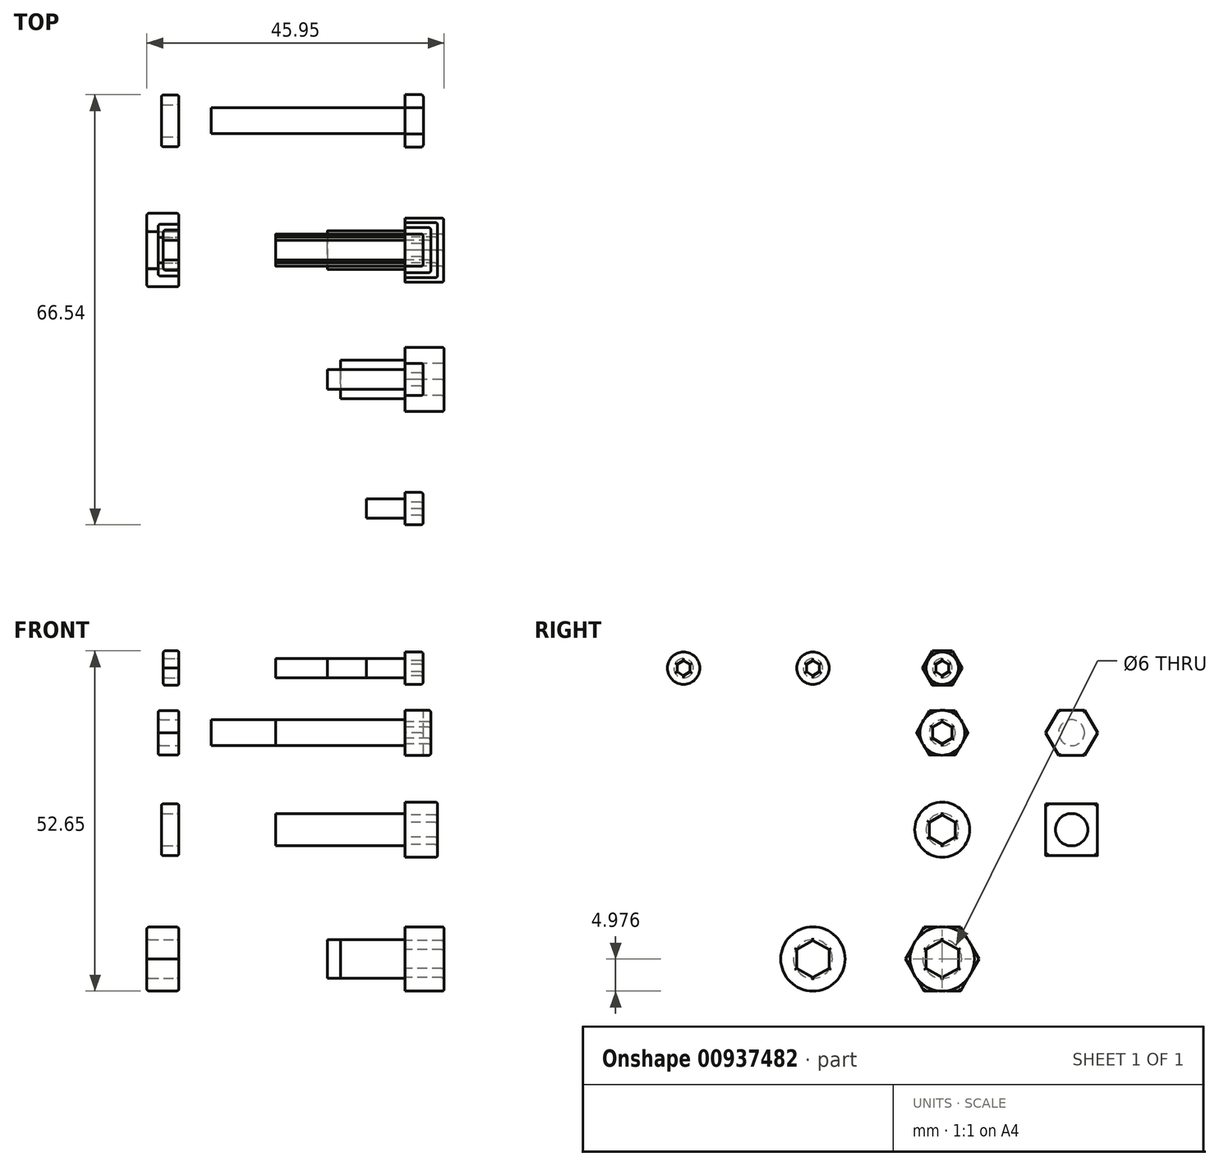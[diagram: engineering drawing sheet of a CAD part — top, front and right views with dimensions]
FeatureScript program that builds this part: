
annotation { "Feature Type Name" : "Feature", "Feature Type Description" : "" }
export const myFeature = defineFeature(function(context is Context, id is Id, definition is map)
    precondition{}
    {
        {
            var Q0;
            Q0=qCreatedBy(makeId("Right.planeOp"),FACE);
            var sketch = newSketch(context, id + "F0", { "sketchPlane" : qUnion([Q0])});
            skCircle(sketch, "E0.cCircle", {"center": v(-28.35, 39.66) * mm, "radius": 2.67 * mm, "construction": true});
            skLineSegment(sketch, "E0.0", {"start": v(-26.81, 36.98) * mm, "end": v(-29.9, 36.98) * mm});
            skLineSegment(sketch, "E0.1", {"start": v(-29.9, 36.98) * mm, "end": v(-31.44, 39.66) * mm});
            skLineSegment(sketch, "E0.2", {"start": v(-31.44, 39.66) * mm, "end": v(-29.9, 42.33) * mm});
            skLineSegment(sketch, "E0.3", {"start": v(-29.9, 42.33) * mm, "end": v(-26.81, 42.33) * mm});
            skLineSegment(sketch, "E0.4", {"start": v(-26.81, 42.33) * mm, "end": v(-25.27, 39.66) * mm});
            skLineSegment(sketch, "E0.5", {"start": v(-25.27, 39.66) * mm, "end": v(-26.81, 36.98) * mm});
            skPoint(sketch, "E0.0.midPoint", {"position": v(-28.35, 36.98) * mm});
            skCircle(sketch, "E1.cCircle", {"center": v(-28.35, 29.66) * mm, "radius": 3.45 * mm, "construction": true});
            skLineSegment(sketch, "E1.0", {"start": v(-26.36, 26.2) * mm, "end": v(-30.35, 26.2) * mm});
            skLineSegment(sketch, "E1.1", {"start": v(-30.35, 26.2) * mm, "end": v(-32.34, 29.66) * mm});
            skLineSegment(sketch, "E1.2", {"start": v(-32.34, 29.66) * mm, "end": v(-30.35, 33.1) * mm});
            skLineSegment(sketch, "E1.3", {"start": v(-30.35, 33.1) * mm, "end": v(-26.36, 33.1) * mm});
            skLineSegment(sketch, "E1.4", {"start": v(-26.36, 33.1) * mm, "end": v(-24.37, 29.66) * mm});
            skLineSegment(sketch, "E1.5", {"start": v(-24.37, 29.66) * mm, "end": v(-26.36, 26.2) * mm});
            skPoint(sketch, "E1.0.midPoint", {"position": v(-28.35, 26.2) * mm});
            skCircle(sketch, "E2.cCircle", {"center": v(-28.35, -5.34) * mm, "radius": 4.92 * mm, "construction": true});
            skLineSegment(sketch, "E2.0", {"start": v(-25.51, -10.27) * mm, "end": v(-31.2, -10.27) * mm});
            skLineSegment(sketch, "E2.1", {"start": v(-31.2, -10.27) * mm, "end": v(-34.04, -5.34) * mm});
            skLineSegment(sketch, "E2.2", {"start": v(-34.04, -5.34) * mm, "end": v(-31.2, -0.42) * mm});
            skLineSegment(sketch, "E2.3", {"start": v(-31.2, -0.42) * mm, "end": v(-25.51, -0.42) * mm});
            skLineSegment(sketch, "E2.4", {"start": v(-25.51, -0.42) * mm, "end": v(-22.67, -5.34) * mm});
            skLineSegment(sketch, "E2.5", {"start": v(-22.67, -5.34) * mm, "end": v(-25.51, -10.27) * mm});
            skPoint(sketch, "E2.0.midPoint", {"position": v(-28.35, -10.27) * mm});
            skCircle(sketch, "E3", {"center": v(-28.35, 39.66) * mm, "radius": 1.5 * mm});
            skCircle(sketch, "E4", {"center": v(-28.35, 29.66) * mm, "radius": 2 * mm});
            skCircle(sketch, "E5", {"center": v(-28.35, -5.34) * mm, "radius": 3 * mm});
            skLineSegment(sketch, "E6.bottom", {"start": v(-4.35, 18.66) * mm, "end": v(-12.35, 18.66) * mm});
            skLineSegment(sketch, "E6.top", {"start": v(-4.35, 10.66) * mm, "end": v(-12.35, 10.66) * mm});
            skLineSegment(sketch, "E6.left", {"start": v(-4.35, 18.66) * mm, "end": v(-4.35, 10.66) * mm});
            skLineSegment(sketch, "E6.right", {"start": v(-12.35, 18.66) * mm, "end": v(-12.35, 10.66) * mm});
            skCircle(sketch, "E7", {"center": v(-8.35, 14.66) * mm, "radius": 2.5 * mm});
            skLineSegment(sketch, "E8", {"start": v(-28.35, 48.47) * mm, "end": v(-28.35, -22.46) * mm, "construction": true});
            skLineSegment(sketch, "E9", {"start": v(-8.35, 48.47) * mm, "end": v(-8.35, -22.46) * mm, "construction": true});
            skPoint(sketch, "E10", {"position": v(-28.35, 14.66) * mm});
            skSolve(sketch);
        }
        {
            var Q0;
            Q0=makeQuery(id+"F0.imprint","IMPRINT",FACE,{"disambiguationData":[TD([[makeQuery(id+"F0.imprint","IMPRINT",EDGE,{"derivedFrom":sQuery(id+"F0.wireOp",EDGE,"E0.0")}),-1.0]])]});
            extrude(context, id + "F1", {"entities" : qUnion([Q0]), "oppositeDirection" : true, "depth" : 2.4 * mm, "offsetDistance" : 25 * mm});
        }
        {
            var Q0;
            Q0=makeQuery(id+"F0.imprint","IMPRINT",FACE,{"disambiguationData":[TD([[makeQuery(id+"F0.imprint","IMPRINT",EDGE,{"derivedFrom":sQuery(id+"F0.wireOp",EDGE,"E1.0")}),-1.0]])]});
            extrude(context, id + "F2", {"entities" : qUnion([Q0]), "oppositeDirection" : true, "depth" : 3.2 * mm, "offsetDistance" : 25 * mm});
        }
        {
            var Q0;
            Q0=makeQuery(id+"F0.imprint","IMPRINT",FACE,{"disambiguationData":[TD([[makeQuery(id+"F0.imprint","IMPRINT",EDGE,{"derivedFrom":sQuery(id+"F0.wireOp",EDGE,"E2.0")}),-1.0]])]});
            extrude(context, id + "F3", {"entities" : qUnion([Q0]), "oppositeDirection" : true, "depth" : 4.95 * mm, "offsetDistance" : 25 * mm});
        }
        {
            var Q0;
            Q0=makeQuery(id+"F0.imprint","IMPRINT",FACE,{"disambiguationData":[TD([[makeQuery(id+"F0.imprint","IMPRINT",EDGE,{"derivedFrom":sQuery(id+"F0.wireOp",EDGE,"E6.bottom")}),1.0]])]});
            extrude(context, id + "F4", {"entities" : qUnion([Q0]), "oppositeDirection" : true, "depth" : 2.7 * mm, "offsetDistance" : 25 * mm});
        }
        {
            var Q0;
            Q0=qCreatedBy(makeId("Right.planeOp"),FACE);
            cPlane(context, id + "F5", {"entities" : qUnion([Q0]), "cplaneType" : CPlaneType.OFFSET, "offset" : 35 * mm, "width" : 150 * mm, "height" : 150 * mm});
        }
        {
            var Q0;
            Q0=qCreatedBy(id+"F5.planeOp",FACE);
            var sketch = newSketch(context, id + "F6", { "sketchPlane" : qUnion([Q0])});
            skPoint(sketch, "E11.0", {"position": v(-28.35, 39.66) * mm});
            skPoint(sketch, "E11.1", {"position": v(-28.35, 29.66) * mm});
            skPoint(sketch, "E11.2", {"position": v(-28.35, -5.34) * mm});
            skCircle(sketch, "E12", {"center": v(-28.35, 39.66) * mm, "radius": 1.5 * mm});
            skCircle(sketch, "E13", {"center": v(-28.35, 29.66) * mm, "radius": 2 * mm});
            skCircle(sketch, "E14", {"center": v(-28.35, -5.34) * mm, "radius": 3 * mm});
            skCircle(sketch, "E15", {"center": v(-28.35, 39.66) * mm, "radius": 2.5 * mm});
            skCircle(sketch, "E16", {"center": v(-28.35, 29.66) * mm, "radius": 3.48 * mm});
            skCircle(sketch, "E17", {"center": v(-28.35, -5.34) * mm, "radius": 4.97 * mm});
            skCircle(sketch, "E18.cCircle", {"center": v(-28.35, -5.34) * mm, "radius": 2.5 * mm, "construction": true});
            skLineSegment(sketch, "E18.0", {"start": v(-25.85, -3.9) * mm, "end": v(-25.85, -6.79) * mm});
            skLineSegment(sketch, "E18.1", {"start": v(-25.85, -6.79) * mm, "end": v(-28.35, -8.23) * mm});
            skLineSegment(sketch, "E18.2", {"start": v(-28.35, -8.23) * mm, "end": v(-30.85, -6.79) * mm});
            skLineSegment(sketch, "E18.3", {"start": v(-30.85, -6.79) * mm, "end": v(-30.85, -3.9) * mm});
            skLineSegment(sketch, "E18.4", {"start": v(-30.85, -3.9) * mm, "end": v(-28.35, -2.46) * mm});
            skLineSegment(sketch, "E18.5", {"start": v(-28.35, -2.46) * mm, "end": v(-25.85, -3.9) * mm});
            skPoint(sketch, "E18.0.midPoint", {"position": v(-25.85, -5.34) * mm});
            skCircle(sketch, "E19.cCircle", {"center": v(-28.35, 29.66) * mm, "radius": 1.5 * mm, "construction": true});
            skLineSegment(sketch, "E19.0", {"start": v(-26.85, 30.52) * mm, "end": v(-26.85, 28.79) * mm});
            skLineSegment(sketch, "E19.1", {"start": v(-26.85, 28.79) * mm, "end": v(-28.35, 27.92) * mm});
            skLineSegment(sketch, "E19.2", {"start": v(-28.35, 27.92) * mm, "end": v(-29.85, 28.79) * mm});
            skLineSegment(sketch, "E19.3", {"start": v(-29.85, 28.79) * mm, "end": v(-29.85, 30.52) * mm});
            skLineSegment(sketch, "E19.4", {"start": v(-29.85, 30.52) * mm, "end": v(-28.35, 31.39) * mm});
            skLineSegment(sketch, "E19.5", {"start": v(-28.35, 31.39) * mm, "end": v(-26.85, 30.52) * mm});
            skPoint(sketch, "E19.0.midPoint", {"position": v(-26.85, 29.66) * mm});
            skCircle(sketch, "E20.cCircle", {"center": v(-28.35, 39.66) * mm, "radius": 1 * mm, "construction": true});
            skLineSegment(sketch, "E20.0", {"start": v(-27.35, 40.23) * mm, "end": v(-27.35, 39.08) * mm});
            skLineSegment(sketch, "E20.1", {"start": v(-27.35, 39.08) * mm, "end": v(-28.35, 38.5) * mm});
            skLineSegment(sketch, "E20.2", {"start": v(-28.35, 38.5) * mm, "end": v(-29.35, 39.08) * mm});
            skLineSegment(sketch, "E20.3", {"start": v(-29.35, 39.08) * mm, "end": v(-29.35, 40.23) * mm});
            skLineSegment(sketch, "E20.4", {"start": v(-29.35, 40.23) * mm, "end": v(-28.35, 40.81) * mm});
            skLineSegment(sketch, "E20.5", {"start": v(-28.35, 40.81) * mm, "end": v(-27.35, 40.23) * mm});
            skPoint(sketch, "E20.0.midPoint", {"position": v(-27.35, 39.66) * mm});
            skPoint(sketch, "E21", {"position": v(-8.35, 29.66) * mm});
            skCircle(sketch, "E22", {"center": v(-8.35, 29.66) * mm, "radius": 2 * mm});
            skCircle(sketch, "E23.cCircle", {"center": v(-8.35, 29.66) * mm, "radius": 3.5 * mm, "construction": true});
            skLineSegment(sketch, "E23.0", {"start": v(-10.38, 33.16) * mm, "end": v(-6.33, 33.16) * mm});
            skLineSegment(sketch, "E23.1", {"start": v(-6.33, 33.16) * mm, "end": v(-4.31, 29.66) * mm});
            skLineSegment(sketch, "E23.2", {"start": v(-4.31, 29.66) * mm, "end": v(-6.33, 26.16) * mm});
            skLineSegment(sketch, "E23.3", {"start": v(-6.33, 26.16) * mm, "end": v(-10.38, 26.16) * mm});
            skLineSegment(sketch, "E23.4", {"start": v(-10.38, 26.16) * mm, "end": v(-12.4, 29.66) * mm});
            skLineSegment(sketch, "E23.5", {"start": v(-12.4, 29.66) * mm, "end": v(-10.38, 33.16) * mm});
            skPoint(sketch, "E23.0.midPoint", {"position": v(-8.35, 33.16) * mm});
            skPoint(sketch, "E24.0", {"position": v(-8.35, 14.66) * mm});
            skPoint(sketch, "E25.0", {"position": v(-28.35, 14.66) * mm});
            skCircle(sketch, "E26", {"center": v(-28.35, 14.66) * mm, "radius": 2.5 * mm});
            skCircle(sketch, "E27", {"center": v(-28.35, 14.66) * mm, "radius": 4.25 * mm});
            skCircle(sketch, "E28.cCircle", {"center": v(-28.35, 14.66) * mm, "radius": 2 * mm, "construction": true});
            skLineSegment(sketch, "E28.0", {"start": v(-26.35, 15.81) * mm, "end": v(-26.35, 13.5) * mm});
            skLineSegment(sketch, "E28.1", {"start": v(-26.35, 13.5) * mm, "end": v(-28.35, 12.35) * mm});
            skLineSegment(sketch, "E28.2", {"start": v(-28.35, 12.35) * mm, "end": v(-30.35, 13.5) * mm});
            skLineSegment(sketch, "E28.3", {"start": v(-30.35, 13.5) * mm, "end": v(-30.35, 15.81) * mm});
            skLineSegment(sketch, "E28.4", {"start": v(-30.35, 15.81) * mm, "end": v(-28.35, 16.96) * mm});
            skLineSegment(sketch, "E28.5", {"start": v(-28.35, 16.96) * mm, "end": v(-26.35, 15.81) * mm});
            skPoint(sketch, "E28.0.midPoint", {"position": v(-26.35, 14.66) * mm});
            skPoint(sketch, "E29.0", {"position": v(-48.35, 39.66) * mm});
            skCircle(sketch, "E30", {"center": v(-48.35, 39.66) * mm, "radius": 1.5 * mm});
            skCircle(sketch, "E31", {"center": v(-48.35, 39.66) * mm, "radius": 2.5 * mm});
            skCircle(sketch, "E32.cCircle", {"center": v(-48.35, 39.66) * mm, "radius": 1 * mm, "construction": true});
            skLineSegment(sketch, "E32.0", {"start": v(-47.35, 40.23) * mm, "end": v(-47.35, 39.08) * mm});
            skLineSegment(sketch, "E32.1", {"start": v(-47.35, 39.08) * mm, "end": v(-48.35, 38.5) * mm});
            skLineSegment(sketch, "E32.2", {"start": v(-48.35, 38.5) * mm, "end": v(-49.35, 39.08) * mm});
            skLineSegment(sketch, "E32.3", {"start": v(-49.35, 39.08) * mm, "end": v(-49.35, 40.23) * mm});
            skLineSegment(sketch, "E32.4", {"start": v(-49.35, 40.23) * mm, "end": v(-48.35, 40.81) * mm});
            skLineSegment(sketch, "E32.5", {"start": v(-48.35, 40.81) * mm, "end": v(-47.35, 40.23) * mm});
            skPoint(sketch, "E32.0.midPoint", {"position": v(-47.35, 39.66) * mm});
            skPoint(sketch, "E33.2", {"position": v(-48.35, -5.34) * mm});
            skCircle(sketch, "E34", {"center": v(-48.35, -5.34) * mm, "radius": 3 * mm});
            skCircle(sketch, "E35", {"center": v(-48.35, -5.34) * mm, "radius": 4.97 * mm});
            skCircle(sketch, "E36.cCircle", {"center": v(-48.35, -5.34) * mm, "radius": 2.5 * mm, "construction": true});
            skLineSegment(sketch, "E36.0", {"start": v(-45.85, -3.9) * mm, "end": v(-45.85, -6.79) * mm});
            skLineSegment(sketch, "E36.1", {"start": v(-45.85, -6.79) * mm, "end": v(-48.35, -8.23) * mm});
            skLineSegment(sketch, "E36.2", {"start": v(-48.35, -8.23) * mm, "end": v(-50.85, -6.79) * mm});
            skLineSegment(sketch, "E36.3", {"start": v(-50.85, -6.79) * mm, "end": v(-50.85, -3.9) * mm});
            skLineSegment(sketch, "E36.4", {"start": v(-50.85, -3.9) * mm, "end": v(-48.35, -2.46) * mm});
            skLineSegment(sketch, "E36.5", {"start": v(-48.35, -2.46) * mm, "end": v(-45.85, -3.9) * mm});
            skPoint(sketch, "E36.0.midPoint", {"position": v(-45.85, -5.34) * mm});
            skPoint(sketch, "E37", {"position": v(-30.85, -5.34) * mm});
            skPoint(sketch, "E38.0", {"position": v(-68.35, 39.66) * mm});
            skCircle(sketch, "E39", {"center": v(-68.35, 39.66) * mm, "radius": 1.5 * mm});
            skCircle(sketch, "E40", {"center": v(-68.35, 39.66) * mm, "radius": 2.5 * mm});
            skCircle(sketch, "E41.cCircle", {"center": v(-68.35, 39.66) * mm, "radius": 1 * mm, "construction": true});
            skLineSegment(sketch, "E41.0", {"start": v(-67.35, 40.23) * mm, "end": v(-67.35, 39.08) * mm});
            skLineSegment(sketch, "E41.1", {"start": v(-67.35, 39.08) * mm, "end": v(-68.35, 38.5) * mm});
            skLineSegment(sketch, "E41.2", {"start": v(-68.35, 38.5) * mm, "end": v(-69.35, 39.08) * mm});
            skLineSegment(sketch, "E41.3", {"start": v(-69.35, 39.08) * mm, "end": v(-69.35, 40.23) * mm});
            skLineSegment(sketch, "E41.4", {"start": v(-69.35, 40.23) * mm, "end": v(-68.35, 40.81) * mm});
            skLineSegment(sketch, "E41.5", {"start": v(-68.35, 40.81) * mm, "end": v(-67.35, 40.23) * mm});
            skPoint(sketch, "E41.0.midPoint", {"position": v(-67.35, 39.66) * mm});
            skSolve(sketch);
        }
        {
            var Q0;
            Q0=makeQuery(id+"F6.imprint","IMPRINT",FACE,{"disambiguationData":[TD([[makeQuery(id+"F6.imprint","IMPRINT",EDGE,{"derivedFrom":sQuery(id+"F6.wireOp",EDGE,"E12")}),1.0]])]});
            var Q1;
            Q1=makeQuery(id+"F6.imprint","IMPRINT",FACE,{"disambiguationData":[TD([[makeQuery(id+"F6.imprint","IMPRINT",EDGE,{"derivedFrom":sQuery(id+"F6.wireOp",EDGE,"E20.0")}),-1.0]])]});
            extrude(context, id + "F7", {"entities" : qUnion([Q0, Q1]), "oppositeDirection" : true, "depth" : 20 * mm, "offsetDistance" : 25 * mm});
        }
        {
            var Q0;
            Q0=makeQuery(id+"F6.imprint","IMPRINT",FACE,{"disambiguationData":[TD([[makeQuery(id+"F6.imprint","IMPRINT",EDGE,{"derivedFrom":sQuery(id+"F6.wireOp",EDGE,"E13")}),1.0]])]});
            var Q1;
            Q1=makeQuery(id+"F6.imprint","IMPRINT",FACE,{"disambiguationData":[TD([[makeQuery(id+"F6.imprint","IMPRINT",EDGE,{"derivedFrom":sQuery(id+"F6.wireOp",EDGE,"E19.0")}),-1.0]])]});
            extrude(context, id + "F8", {"entities" : qUnion([Q0, Q1]), "oppositeDirection" : true, "depth" : 20 * mm, "offsetDistance" : 25 * mm});
        }
        {
            var Q0;
            Q0=makeQuery(id+"F6.imprint","IMPRINT",FACE,{"disambiguationData":[TD([[makeQuery(id+"F6.imprint","IMPRINT",EDGE,{"derivedFrom":sQuery(id+"F6.wireOp",EDGE,"E18.0")}),-1.0]])]});
            var Q1;
            Q1=makeQuery(id+"F6.imprint","IMPRINT",FACE,{"disambiguationData":[TD([[makeQuery(id+"F6.imprint","IMPRINT",EDGE,{"derivedFrom":sQuery(id+"F6.wireOp",EDGE,"E14")}),1.0]])]});
            extrude(context, id + "F9", {"entities" : qUnion([Q0, Q1]), "flatOperationType" : FlatOperationType.REMOVE, "oppositeDirection" : true, "depth" : 12 * mm, "offsetDistance" : 25 * mm, "domain" : OperationDomain.MODEL});
        }
        {
            var Q0;
            Q0=makeQuery(id+"F6.imprint","IMPRINT",FACE,{"disambiguationData":[TD([[makeQuery(id+"F6.imprint","IMPRINT",EDGE,{"derivedFrom":sQuery(id+"F6.wireOp",EDGE,"E12")}),-1.0]])]});
            var Q1;
            Q1=makeQuery(id+"F6.imprint","IMPRINT",FACE,{"disambiguationData":[TD([[makeQuery(id+"F6.imprint","IMPRINT",EDGE,{"derivedFrom":sQuery(id+"F6.wireOp",EDGE,"E12")}),1.0]])]});
            extrude(context, id + "F10", {"entities" : qUnion([Q0, Q1]), "operationType" : NewBodyOperationType.ADD, "flatOperationType" : FlatOperationType.REMOVE, "depth" : 2.75 * mm, "offsetDistance" : 25 * mm, "domain" : OperationDomain.MODEL});
        }
        {
            var Q0;
            Q0=makeQuery(id+"F6.imprint","IMPRINT",FACE,{"disambiguationData":[TD([[makeQuery(id+"F6.imprint","IMPRINT",EDGE,{"derivedFrom":sQuery(id+"F6.wireOp",EDGE,"E13")}),1.0]])]});
            var Q1;
            Q1=makeQuery(id+"F6.imprint","IMPRINT",FACE,{"disambiguationData":[TD([[makeQuery(id+"F6.imprint","IMPRINT",EDGE,{"derivedFrom":sQuery(id+"F6.wireOp",EDGE,"E13")}),-1.0]])]});
            extrude(context, id + "F11", {"entities" : qUnion([Q0, Q1]), "operationType" : NewBodyOperationType.ADD, "flatOperationType" : FlatOperationType.REMOVE, "depth" : 3.95 * mm, "offsetDistance" : 25 * mm, "domain" : OperationDomain.MODEL});
        }
        {
            var Q0;
            Q0=makeQuery(id+"F6.imprint","IMPRINT",FACE,{"disambiguationData":[TD([[makeQuery(id+"F6.imprint","IMPRINT",EDGE,{"derivedFrom":sQuery(id+"F6.wireOp",EDGE,"E14")}),1.0]])]});
            var Q1;
            Q1=makeQuery(id+"F6.imprint","IMPRINT",FACE,{"disambiguationData":[TD([[makeQuery(id+"F6.imprint","IMPRINT",EDGE,{"derivedFrom":sQuery(id+"F6.wireOp",EDGE,"E14")}),-1.0]])]});
            extrude(context, id + "F12", {"entities" : qUnion([Q0, Q1]), "operationType" : NewBodyOperationType.ADD, "depth" : 5.95 * mm, "offsetDistance" : 25 * mm});
        }
        {
            var Q0;
            Q0=makeQuery(id+"F6.imprint","IMPRINT",FACE,{"disambiguationData":[TD([[makeQuery(id+"F6.imprint","IMPRINT",EDGE,{"derivedFrom":sQuery(id+"F6.wireOp",EDGE,"E22")}),1.0]])]});
            var Q1;
            Q1=makeQuery(id+"F6.imprint","IMPRINT",FACE,{"disambiguationData":[TD([[makeQuery(id+"F6.imprint","IMPRINT",EDGE,{"derivedFrom":sQuery(id+"F6.wireOp",EDGE,"E22")}),-1.0]])]});
            extrude(context, id + "F13", {"entities" : qUnion([Q0, Q1]), "depth" : 2.8 * mm, "offsetDistance" : 25 * mm});
        }
        {
            var Q0;
            Q0=makeQuery(id+"F6.imprint","IMPRINT",FACE,{"disambiguationData":[TD([[makeQuery(id+"F6.imprint","IMPRINT",EDGE,{"derivedFrom":sQuery(id+"F6.wireOp",EDGE,"E22")}),1.0]])]});
            extrude(context, id + "F14", {"entities" : qUnion([Q0]), "operationType" : NewBodyOperationType.ADD, "oppositeDirection" : true, "depth" : 30 * mm, "offsetDistance" : 25 * mm});
        }
        {
            var Q0;
            Q0=makeQuery(id+"F6.imprint","IMPRINT",FACE,{"disambiguationData":[TD([[makeQuery(id+"F6.imprint","IMPRINT",EDGE,{"derivedFrom":sQuery(id+"F6.wireOp",EDGE,"E26")}),-1.0]])]});
            var Q1;
            Q1=makeQuery(id+"F6.imprint","IMPRINT",FACE,{"disambiguationData":[TD([[makeQuery(id+"F6.imprint","IMPRINT",EDGE,{"derivedFrom":sQuery(id+"F6.wireOp",EDGE,"E26")}),1.0]])]});
            extrude(context, id + "F15", {"entities" : qUnion([Q0, Q1]), "depth" : 5 * mm, "offsetDistance" : 25 * mm});
        }
        {
            var Q0;
            Q0=makeQuery(id+"F6.imprint","IMPRINT",FACE,{"disambiguationData":[TD([[makeQuery(id+"F6.imprint","IMPRINT",EDGE,{"derivedFrom":sQuery(id+"F6.wireOp",EDGE,"E26")}),1.0]])]});
            var Q1;
            Q1=makeQuery(id+"F6.imprint","IMPRINT",FACE,{"disambiguationData":[TD([[makeQuery(id+"F6.imprint","IMPRINT",EDGE,{"derivedFrom":sQuery(id+"F6.wireOp",EDGE,"E28.0")}),-1.0]])]});
            extrude(context, id + "F16", {"entities" : qUnion([Q0, Q1]), "operationType" : NewBodyOperationType.ADD, "oppositeDirection" : true, "depth" : 20 * mm, "offsetDistance" : 25 * mm});
        }
        {
            var Q0;
            Q0=makeQuery(id+"F6.imprint","IMPRINT",FACE,{"disambiguationData":[TD([[makeQuery(id+"F6.imprint","IMPRINT",EDGE,{"derivedFrom":sQuery(id+"F6.wireOp",EDGE,"E32.0")}),-1.0]])]});
            var Q1;
            Q1=makeQuery(id+"F6.imprint","IMPRINT",FACE,{"disambiguationData":[TD([[makeQuery(id+"F6.imprint","IMPRINT",EDGE,{"derivedFrom":sQuery(id+"F6.wireOp",EDGE,"E30")}),1.0]])]});
            extrude(context, id + "F17", {"entities" : qUnion([Q0, Q1]), "oppositeDirection" : true, "depth" : 12 * mm, "offsetDistance" : 25 * mm});
        }
        {
            var Q0;
            Q0=makeQuery(id+"F6.imprint","IMPRINT",FACE,{"disambiguationData":[TD([[makeQuery(id+"F6.imprint","IMPRINT",EDGE,{"derivedFrom":sQuery(id+"F6.wireOp",EDGE,"E30")}),1.0]])]});
            var Q1;
            Q1=makeQuery(id+"F6.imprint","IMPRINT",FACE,{"disambiguationData":[TD([[makeQuery(id+"F6.imprint","IMPRINT",EDGE,{"derivedFrom":sQuery(id+"F6.wireOp",EDGE,"E30")}),-1.0]])]});
            extrude(context, id + "F18", {"entities" : qUnion([Q0, Q1]), "operationType" : NewBodyOperationType.ADD, "depth" : 2.75 * mm, "offsetDistance" : 25 * mm});
        }
        {
            var Q0;
            Q0=makeQuery(id+"F6.imprint","IMPRINT",FACE,{"disambiguationData":[TD([[makeQuery(id+"F6.imprint","IMPRINT",EDGE,{"derivedFrom":sQuery(id+"F6.wireOp",EDGE,"E36.0")}),-1.0]])]});
            var Q1;
            Q1=makeQuery(id+"F6.imprint","IMPRINT",FACE,{"disambiguationData":[TD([[makeQuery(id+"F6.imprint","IMPRINT",EDGE,{"derivedFrom":sQuery(id+"F6.wireOp",EDGE,"E34")}),1.0]])]});
            extrude(context, id + "F19", {"entities" : qUnion([Q0, Q1]), "oppositeDirection" : true, "depth" : 10 * mm, "offsetDistance" : 25 * mm});
        }
        {
            var Q0;
            Q0=makeQuery(id+"F6.imprint","IMPRINT",FACE,{"disambiguationData":[TD([[makeQuery(id+"F6.imprint","IMPRINT",EDGE,{"derivedFrom":sQuery(id+"F6.wireOp",EDGE,"E34")}),1.0]])]});
            var Q1;
            Q1=makeQuery(id+"F6.imprint","IMPRINT",FACE,{"disambiguationData":[TD([[makeQuery(id+"F6.imprint","IMPRINT",EDGE,{"derivedFrom":sQuery(id+"F6.wireOp",EDGE,"E34")}),-1.0]])]});
            extrude(context, id + "F20", {"entities" : qUnion([Q0, Q1]), "operationType" : NewBodyOperationType.ADD, "depth" : 6 * mm, "offsetDistance" : 25 * mm});
        }
        {
            var Q0;
            Q0=makeQuery(id+"F6.imprint","IMPRINT",FACE,{"disambiguationData":[TD([[makeQuery(id+"F6.imprint","IMPRINT",EDGE,{"derivedFrom":sQuery(id+"F6.wireOp",EDGE,"E41.0")}),-1.0]])]});
            var Q1;
            Q1=makeQuery(id+"F6.imprint","IMPRINT",FACE,{"disambiguationData":[TD([[makeQuery(id+"F6.imprint","IMPRINT",EDGE,{"derivedFrom":sQuery(id+"F6.wireOp",EDGE,"E39")}),1.0]])]});
            extrude(context, id + "F21", {"entities" : qUnion([Q0, Q1]), "oppositeDirection" : true, "depth" : 6 * mm, "offsetDistance" : 25 * mm});
        }
        {
            var Q0;
            Q0=makeQuery(id+"F6.imprint","IMPRINT",FACE,{"disambiguationData":[TD([[makeQuery(id+"F6.imprint","IMPRINT",EDGE,{"derivedFrom":sQuery(id+"F6.wireOp",EDGE,"E39")}),1.0]])]});
            var Q1;
            Q1=makeQuery(id+"F6.imprint","IMPRINT",FACE,{"disambiguationData":[TD([[makeQuery(id+"F6.imprint","IMPRINT",EDGE,{"derivedFrom":sQuery(id+"F6.wireOp",EDGE,"E39")}),-1.0]])]});
            extrude(context, id + "F22", {"entities" : qUnion([Q0, Q1]), "operationType" : NewBodyOperationType.ADD, "depth" : 2.75 * mm, "offsetDistance" : 25 * mm});
        }
        {
            var Q0;
            Q0=makeQuery(id+"F2.opExtrude","CAP_FACE",FACE,{"disambiguationData":[OSD([sQuery(id+"F0.wireOp",EDGE,"E1.0"),sQuery(id+"F0.wireOp",EDGE,"E1.1"),sQuery(id+"F0.wireOp",EDGE,"E1.2"),sQuery(id+"F0.wireOp",EDGE,"E1.3"),sQuery(id+"F0.wireOp",EDGE,"E1.4"),sQuery(id+"F0.wireOp",EDGE,"E1.5"),sQuery(id+"F0.wireOp",EDGE,"E4")])],"isStart":false});
            var Q1;
            Q1=makeQuery(id+"F3.opExtrude","CAP_FACE",FACE,{"disambiguationData":[OSD([sQuery(id+"F0.wireOp",EDGE,"E2.0"),sQuery(id+"F0.wireOp",EDGE,"E2.1"),sQuery(id+"F0.wireOp",EDGE,"E2.2"),sQuery(id+"F0.wireOp",EDGE,"E2.3"),sQuery(id+"F0.wireOp",EDGE,"E2.4"),sQuery(id+"F0.wireOp",EDGE,"E2.5"),sQuery(id+"F0.wireOp",EDGE,"E5")])],"isStart":false});
            var Q2;
            Q2=makeQuery(id+"F2.opExtrude","CAP_FACE",FACE,{"disambiguationData":[OSD([sQuery(id+"F0.wireOp",EDGE,"E1.0"),sQuery(id+"F0.wireOp",EDGE,"E1.1"),sQuery(id+"F0.wireOp",EDGE,"E1.2"),sQuery(id+"F0.wireOp",EDGE,"E1.3"),sQuery(id+"F0.wireOp",EDGE,"E1.4"),sQuery(id+"F0.wireOp",EDGE,"E1.5"),sQuery(id+"F0.wireOp",EDGE,"E4")])],"isStart":true});
            var Q3;
            Q3=makeQuery(id+"F3.opExtrude","CAP_FACE",FACE,{"disambiguationData":[OSD([sQuery(id+"F0.wireOp",EDGE,"E2.0"),sQuery(id+"F0.wireOp",EDGE,"E2.1"),sQuery(id+"F0.wireOp",EDGE,"E2.2"),sQuery(id+"F0.wireOp",EDGE,"E2.3"),sQuery(id+"F0.wireOp",EDGE,"E2.4"),sQuery(id+"F0.wireOp",EDGE,"E2.5"),sQuery(id+"F0.wireOp",EDGE,"E5")])],"isStart":true});
            var Q4;
            Q4=makeQuery(id+"F4.opExtrude","CAP_FACE",FACE,{"disambiguationData":[OSD([sQuery(id+"F0.wireOp",EDGE,"E6.bottom"),sQuery(id+"F0.wireOp",EDGE,"E6.top"),sQuery(id+"F0.wireOp",EDGE,"E6.left"),sQuery(id+"F0.wireOp",EDGE,"E6.right"),sQuery(id+"F0.wireOp",EDGE,"E7")])],"isStart":true});
            var Q5;
            Q5=makeQuery(id+"F4.opExtrude","CAP_FACE",FACE,{"disambiguationData":[OSD([sQuery(id+"F0.wireOp",EDGE,"E6.bottom"),sQuery(id+"F0.wireOp",EDGE,"E6.top"),sQuery(id+"F0.wireOp",EDGE,"E6.left"),sQuery(id+"F0.wireOp",EDGE,"E6.right"),sQuery(id+"F0.wireOp",EDGE,"E7")])],"isStart":false});
            var Q6;
            Q6=makeQuery(id+"F1.opExtrude","CAP_FACE",FACE,{"disambiguationData":[OSD([sQuery(id+"F0.wireOp",EDGE,"E0.0"),sQuery(id+"F0.wireOp",EDGE,"E0.1"),sQuery(id+"F0.wireOp",EDGE,"E0.2"),sQuery(id+"F0.wireOp",EDGE,"E0.3"),sQuery(id+"F0.wireOp",EDGE,"E0.4"),sQuery(id+"F0.wireOp",EDGE,"E0.5"),sQuery(id+"F0.wireOp",EDGE,"E3")])],"isStart":true});
            var Q7;
            Q7=makeQuery(id+"F1.opExtrude","CAP_FACE",FACE,{"disambiguationData":[OSD([sQuery(id+"F0.wireOp",EDGE,"E0.0"),sQuery(id+"F0.wireOp",EDGE,"E0.1"),sQuery(id+"F0.wireOp",EDGE,"E0.2"),sQuery(id+"F0.wireOp",EDGE,"E0.3"),sQuery(id+"F0.wireOp",EDGE,"E0.4"),sQuery(id+"F0.wireOp",EDGE,"E0.5"),sQuery(id+"F0.wireOp",EDGE,"E3")])],"isStart":false});
            var Q8;
            Q8=makeQuery(id+"F22.opExtrude","CAP_FACE",FACE,{"disambiguationData":[OSD([sQuery(id+"F6.wireOp",EDGE,"E40"),sQuery(id+"F6.wireOp",EDGE,"E41.0"),sQuery(id+"F6.wireOp",EDGE,"E41.1"),sQuery(id+"F6.wireOp",EDGE,"E41.2"),sQuery(id+"F6.wireOp",EDGE,"E41.3"),sQuery(id+"F6.wireOp",EDGE,"E41.4"),sQuery(id+"F6.wireOp",EDGE,"E41.5")])],"isStart":false});
            var Q9;
            Q9=makeQuery(id+"F18.opExtrude","CAP_FACE",FACE,{"disambiguationData":[OSD([sQuery(id+"F6.wireOp",EDGE,"E31"),sQuery(id+"F6.wireOp",EDGE,"E32.0"),sQuery(id+"F6.wireOp",EDGE,"E32.1"),sQuery(id+"F6.wireOp",EDGE,"E32.2"),sQuery(id+"F6.wireOp",EDGE,"E32.3"),sQuery(id+"F6.wireOp",EDGE,"E32.4"),sQuery(id+"F6.wireOp",EDGE,"E32.5")])],"isStart":false});
            var Q10;
            Q10=makeQuery(id+"F10.opExtrude","CAP_FACE",FACE,{"disambiguationData":[OSD([sQuery(id+"F6.wireOp",EDGE,"E15"),sQuery(id+"F6.wireOp",EDGE,"E20.0"),sQuery(id+"F6.wireOp",EDGE,"E20.1"),sQuery(id+"F6.wireOp",EDGE,"E20.2"),sQuery(id+"F6.wireOp",EDGE,"E20.3"),sQuery(id+"F6.wireOp",EDGE,"E20.4"),sQuery(id+"F6.wireOp",EDGE,"E20.5")])],"isStart":false});
            var Q11;
            Q11=makeQuery(id+"F11.opExtrude","CAP_FACE",FACE,{"disambiguationData":[OSD([sQuery(id+"F6.wireOp",EDGE,"E16"),sQuery(id+"F6.wireOp",EDGE,"E19.0"),sQuery(id+"F6.wireOp",EDGE,"E19.1"),sQuery(id+"F6.wireOp",EDGE,"E19.2"),sQuery(id+"F6.wireOp",EDGE,"E19.3"),sQuery(id+"F6.wireOp",EDGE,"E19.4"),sQuery(id+"F6.wireOp",EDGE,"E19.5")])],"isStart":false});
            var Q12;
            Q12=makeQuery(id+"F13.opExtrude","CAP_FACE",FACE,{"disambiguationData":[OSD([sQuery(id+"F6.wireOp",EDGE,"E23.0"),sQuery(id+"F6.wireOp",EDGE,"E23.1"),sQuery(id+"F6.wireOp",EDGE,"E23.2"),sQuery(id+"F6.wireOp",EDGE,"E23.3"),sQuery(id+"F6.wireOp",EDGE,"E23.4"),sQuery(id+"F6.wireOp",EDGE,"E23.5")])],"isStart":false});
            var Q13;
            Q13=makeQuery(id+"F15.opExtrude","CAP_FACE",FACE,{"disambiguationData":[OSD([sQuery(id+"F6.wireOp",EDGE,"E27"),sQuery(id+"F6.wireOp",EDGE,"E28.0"),sQuery(id+"F6.wireOp",EDGE,"E28.1"),sQuery(id+"F6.wireOp",EDGE,"E28.2"),sQuery(id+"F6.wireOp",EDGE,"E28.3"),sQuery(id+"F6.wireOp",EDGE,"E28.4"),sQuery(id+"F6.wireOp",EDGE,"E28.5")])],"isStart":false});
            var Q14;
            Q14=makeQuery(id+"F12.opExtrude","CAP_FACE",FACE,{"disambiguationData":[OSD([sQuery(id+"F6.wireOp",EDGE,"E17"),sQuery(id+"F6.wireOp",EDGE,"E18.0"),sQuery(id+"F6.wireOp",EDGE,"E18.1"),sQuery(id+"F6.wireOp",EDGE,"E18.2"),sQuery(id+"F6.wireOp",EDGE,"E18.3"),sQuery(id+"F6.wireOp",EDGE,"E18.4"),sQuery(id+"F6.wireOp",EDGE,"E18.5")])],"isStart":false});
            var Q15;
            Q15=makeQuery(id+"F20.opExtrude","CAP_FACE",FACE,{"disambiguationData":[OSD([sQuery(id+"F6.wireOp",EDGE,"E35"),sQuery(id+"F6.wireOp",EDGE,"E36.0"),sQuery(id+"F6.wireOp",EDGE,"E36.1"),sQuery(id+"F6.wireOp",EDGE,"E36.2"),sQuery(id+"F6.wireOp",EDGE,"E36.3"),sQuery(id+"F6.wireOp",EDGE,"E36.4"),sQuery(id+"F6.wireOp",EDGE,"E36.5")])],"isStart":false});
            fillet(context, id + "F23", {"entities" : qUnion([Q0, Q1, Q2, Q3, Q4, Q5, Q6, Q7, Q8, Q9, Q10, Q11, Q12, Q13, Q14, Q15]), "radius" : 0.3 * mm, "tangentPropagation" : true, "defaultsChanged" : false, "vertexSettings" : [], "allowEdgeOverflow" : false});
        }
    });
